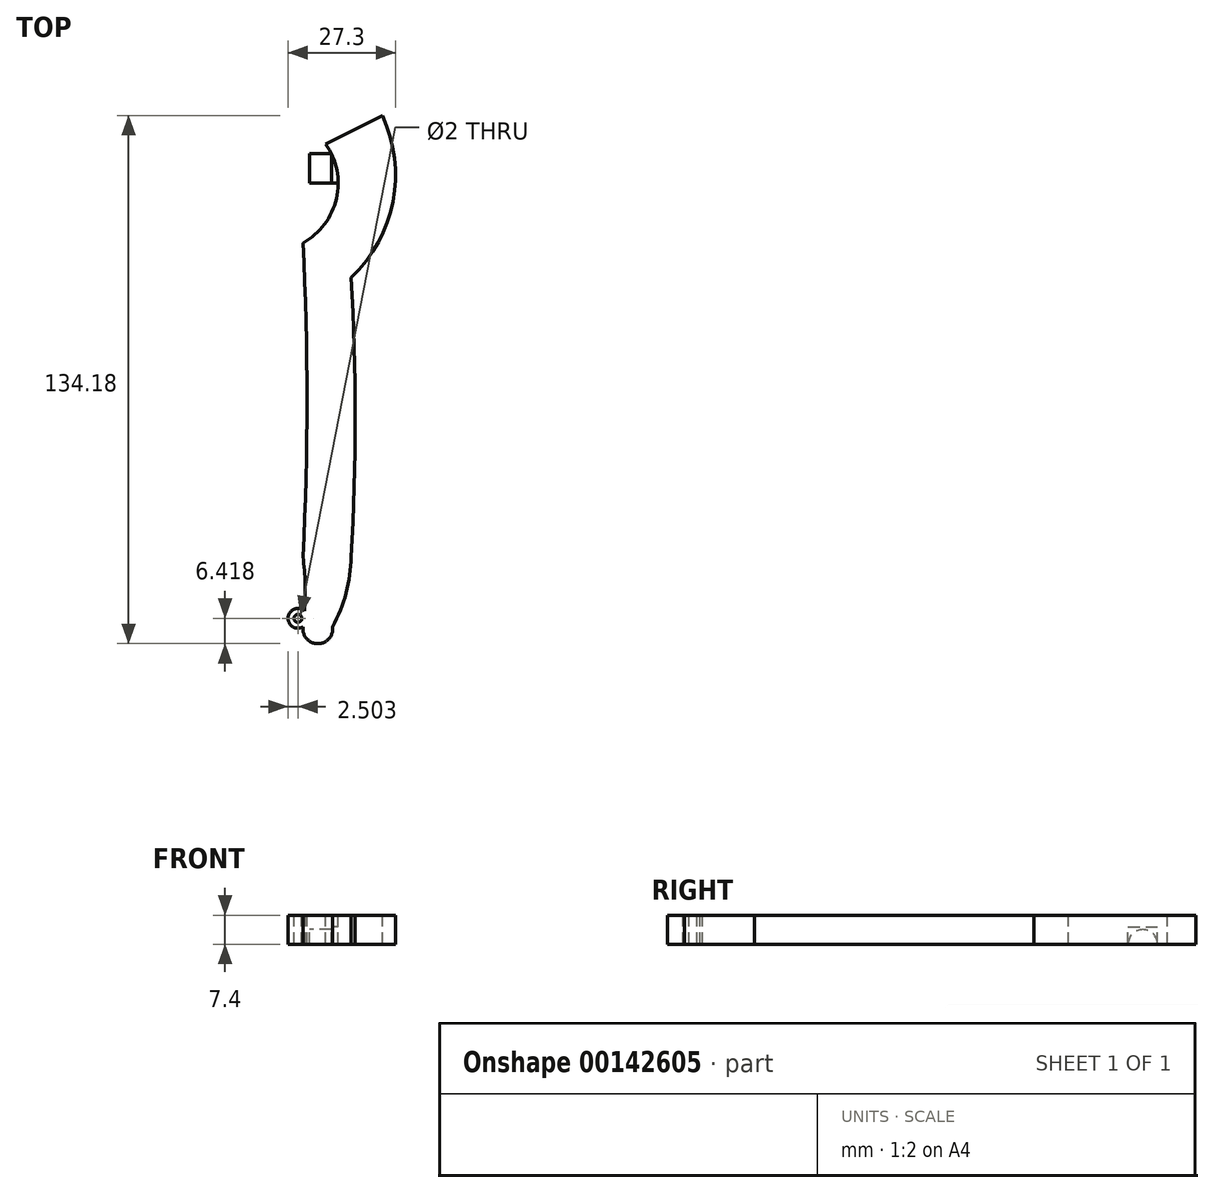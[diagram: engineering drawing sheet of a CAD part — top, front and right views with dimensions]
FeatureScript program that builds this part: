
annotation { "Feature Type Name" : "Feature", "Feature Type Description" : "" }
export const myFeature = defineFeature(function(context is Context, id is Id, definition is map)
    precondition{}
    {
        {
            var Q0;
            Q0=qCreatedBy(makeId("Top.planeOp"),FACE);
            var sketch = newSketch(context, id + "F0", { "sketchPlane" : qUnion([Q0])});
            skArc(sketch, "E0", {"start": v(-18.84, -33.1) * mm, "mid": v(-9.92, -17.2) * mm, "end": v(-18.84, -1.3) * mm});
            skArc(sketch, "E1", {"start": v(-9.22, -40.6) * mm, "mid": v(1.28, -22.3) * mm, "end": v(-0.84, -1.3) * mm});
            skArc(sketch, "E2", {"start": v(-18.84, -111.7) * mm, "mid": v(-17.84, -72.4) * mm, "end": v(-18.84, -33.1) * mm});
            skArc(sketch, "E3", {"start": v(-9.22, -112.4) * mm, "mid": v(-8.2, -76.5) * mm, "end": v(-9.22, -40.6) * mm});
            skArc(sketch, "E4", {"start": v(-18.84, -111.7) * mm, "mid": v(-14.2, -114.48) * mm, "end": v(-9.22, -112.4) * mm});
            skLineSegment(sketch, "E5", {"start": v(-0.84, -1.3) * mm, "end": v(-18.84, -1.3) * mm});
            skArc(sketch, "E6.0", {"start": v(-20.16, -112.1) * mm, "mid": v(-19.14, -72.24) * mm, "end": v(-20.18, -32.37) * mm});
            skLineSegment(sketch, "E6.1", {"start": v(0, 0) * mm, "end": v(-26.43, 0) * mm});
            skArc(sketch, "E6.2", {"start": v(-7.89, -41.14) * mm, "mid": v(2.7, -21.84) * mm, "end": v(0, 0) * mm});
            skArc(sketch, "E6.3", {"start": v(-20.18, -32.37) * mm, "mid": v(-11.53, -13.92) * mm, "end": v(-26.43, 0) * mm});
            skArc(sketch, "E6.4", {"start": v(-7.9, -112.1) * mm, "mid": v(-6.9, -76.62) * mm, "end": v(-7.89, -41.14) * mm});
            skArc(sketch, "E7", {"start": v(-20.16, -129.9) * mm, "mid": v(-19.6, -121) * mm, "end": v(-20.16, -112.1) * mm});
            skArc(sketch, "E8", {"start": v(-12.62, -129.9) * mm, "mid": v(-9.22, -121.28) * mm, "end": v(-7.9, -112.1) * mm});
            skArc(sketch, "E9", {"start": v(-20.16, -129.9) * mm, "mid": v(-16.4, -134.18) * mm, "end": v(-12.62, -129.9) * mm});
            skArc(sketch, "E10", {"start": v(-19.77, -125.92) * mm, "mid": v(-23.95, -127.51) * mm, "end": v(-20.16, -129.9) * mm});
            skCircle(sketch, "E11", {"center": v(-21.46, -127.76) * mm, "radius": 1 * mm});
            skLineSegment(sketch, "E12", {"start": v(-11.22, -17.2) * mm, "end": v(-18.52, -17.2) * mm});
            skLineSegment(sketch, "E13", {"start": v(-18.52, -17.2) * mm, "end": v(-18.52, -9.7) * mm});
            skLineSegment(sketch, "E14", {"start": v(-18.52, -9.7) * mm, "end": v(-12.93, -9.7) * mm});
            skLineSegment(sketch, "E15", {"start": v(0, 0) * mm, "end": v(-14.4, -7.2) * mm});
            skSolve(sketch);
        }
        {
            var Q0;
            {var subQ1=sQuery(id+"F0.wireOp",EDGE,"E1");Q0=makeQuery(id+"F0.imprint","IMPRINT",FACE,{"disambiguationData":[TD([[makeQuery(id+"F0.imprint","IMPRINT",EDGE,{"derivedFrom":subQ1}),1.0]])]});}
            var Q1;
            {var subQ8=sQuery(id+"F0.wireOp",EDGE,"E1");Q1=makeQuery(id+"F0.imprint","IMPRINT",FACE,{"disambiguationData":[TD([[makeQuery(id+"F0.imprint","IMPRINT",EDGE,{"derivedFrom":subQ8}),-1.0]])]});}
            var Q2;
            {var subQ0=sQuery(id+"F0.wireOp",EDGE,"E10");Q2=makeQuery(id+"F0.imprint","IMPRINT",FACE,{"disambiguationData":[TD([[makeQuery(id+"F0.imprint","IMPRINT",EDGE,{"derivedFrom":subQ0}),1.0]])]});}
            extrude(context, id + "F1", {"entities" : qUnion([Q0, Q1, Q2]), "oppositeDirection" : true, "depth" : 8.4 * mm});
        }
        {
            var Q0;
            {var subQ0=sQuery(id+"F0.wireOp",EDGE,"E12");Q0=makeQuery(id+"F0.imprint","IMPRINT",FACE,{"disambiguationData":[TD([[makeQuery(id+"F0.imprint","IMPRINT",EDGE,{"derivedFrom":subQ0}),-1.0]])]});}
            extrude(context, id + "F2", {"entities" : qUnion([Q0]), "operationType" : NewBodyOperationType.ADD, "oppositeDirection" : true, "depth" : 8.4 * mm});
        }
        {
            var Q0;
            {var subQ0=sQuery(id+"F0.wireOp",EDGE,"E12");Q0=makeQuery(id+"F0.imprint","IMPRINT",FACE,{"disambiguationData":[TD([[makeQuery(id+"F0.imprint","IMPRINT",EDGE,{"derivedFrom":subQ0}),-1.0]])]});}
            extrude(context, id + "F3", {"entities" : qUnion([Q0]), "operationType" : NewBodyOperationType.REMOVE, "oppositeDirection" : true, "depth" : 4 * mm});
        }
        {
            var Q0;
            Q0=makeQuery(id+"F2.opExtrude","SWEPT_FACE",FACE,{"disambiguationData":[OSD([sQuery(id+"F0.wireOp",EDGE,"E13")])]});
            var sketch = newSketch(context, id + "F4", { "sketchPlane" : qUnion([Q0])});
            skLineSegment(sketch, "E16.0", {"start": v(17.2, -8.4) * mm, "end": v(9.7, -8.4) * mm});
            skLineSegment(sketch, "E16.1", {"start": v(17.2, -8.4) * mm, "end": v(17.2, -4) * mm});
            skLineSegment(sketch, "E16.2", {"start": v(17.2, -4) * mm, "end": v(9.7, -4) * mm});
            skLineSegment(sketch, "E16.3", {"start": v(9.7, -8.4) * mm, "end": v(9.7, -4) * mm});
            skArc(sketch, "E17", {"start": v(17.2, -8.4) * mm, "mid": v(13.45, -4.65) * mm, "end": v(9.7, -8.4) * mm});
            skSolve(sketch);
        }
        {
            var Q0;
            Q0=makeQuery(id+"F4.imprint","IMPRINT",FACE,{"disambiguationData":[TD([[makeQuery(id+"F4.imprint","IMPRINT",EDGE,{"derivedFrom":sQuery(id+"F4.wireOp",EDGE,"E16.1")}),1.0]])]});
            extrude(context, id + "F5", {"entities" : qUnion([Q0]), "operationType" : NewBodyOperationType.REMOVE, "oppositeDirection" : true, "depth" : 5.6 * mm});
        }
        {
            var Q0;
            {var subQ0=sQuery(id+"F0.wireOp",EDGE,"E6.3");Q0=makeQuery(id+"F2.boolean.opBoolean","MERGE",FACE,{"derivedFrom":[makeQuery(id+"F1.opExtrude","CAP_FACE",FACE,{"disambiguationData":[OSD([sQuery(id+"F0.wireOp",EDGE,"E6.0"),sQuery(id+"F0.wireOp",EDGE,"E6.1"),sQuery(id+"F0.wireOp",EDGE,"E6.2"),subQ0,sQuery(id+"F0.wireOp",EDGE,"E6.4"),sQuery(id+"F0.wireOp",EDGE,"E7"),sQuery(id+"F0.wireOp",EDGE,"E8"),sQuery(id+"F0.wireOp",EDGE,"E9"),sQuery(id+"F0.wireOp",EDGE,"E10"),sQuery(id+"F0.wireOp",EDGE,"E11")])],"isStart":true}),makeQuery(id+"F2.opExtrude","CAP_FACE",FACE,{"disambiguationData":[OSD([subQ0,sQuery(id+"F0.wireOp",EDGE,"E12"),sQuery(id+"F0.wireOp",EDGE,"E13"),sQuery(id+"F0.wireOp",EDGE,"E14")])],"isStart":true})]});}
            var sketch = newSketch(context, id + "F6", { "sketchPlane" : qUnion([Q0])});
            skSolve(sketch);
        }
        {
            var Q0;
            {var subQ5=sQuery(id+"F0.wireOp",EDGE,"E6.0");Q0=makeQuery(id+"F6.imprint","IMPRINT",FACE,{"disambiguationData":[TD([[makeQuery(id+"F6.imprint","IMPRINT",EDGE,{"derivedFrom":makeQuery(id+"F1.opExtrude","CAP_EDGE",EDGE,{"disambiguationData":[OSD([subQ5])],"isStart":true})}),-1.0]])]});}
            extrude(context, id + "F7", {"entities" : qUnion([Q0]), "operationType" : NewBodyOperationType.REMOVE, "oppositeDirection" : true, "depth" : 1 * mm});
        }
    });
